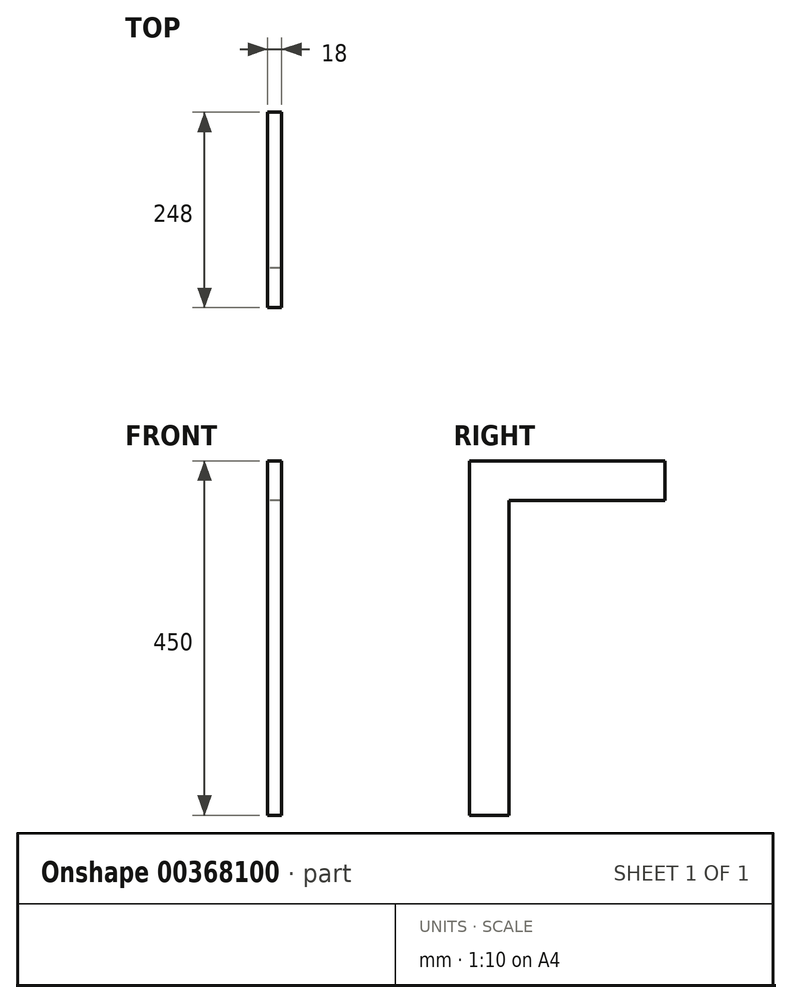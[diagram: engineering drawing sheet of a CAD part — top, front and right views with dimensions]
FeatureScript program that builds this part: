
annotation { "Feature Type Name" : "Feature", "Feature Type Description" : "" }
export const myFeature = defineFeature(function(context is Context, id is Id, definition is map)
    precondition{}
    {
        {
            var Q0;
            Q0=qCreatedBy(makeId("Right.planeOp"),FACE);
            var sketch = newSketch(context, id + "F0", { "sketchPlane" : qUnion([Q0])});
            skLineSegment(sketch, "E0", {"start": v(0, 0) * mm, "end": v(0, 450) * mm});
            skLineSegment(sketch, "E1", {"start": v(0, 450) * mm, "end": v(248, 450) * mm});
            skLineSegment(sketch, "E2", {"start": v(248, 450) * mm, "end": v(248, 400) * mm});
            skLineSegment(sketch, "E3", {"start": v(248, 400) * mm, "end": v(50, 400) * mm});
            skLineSegment(sketch, "E4", {"start": v(50, 400) * mm, "end": v(50, 0) * mm});
            skLineSegment(sketch, "E5", {"start": v(50, 0) * mm, "end": v(0, 0) * mm});
            skSolve(sketch);
        }
        {
            var Q0;
            Q0=makeQuery(id+"F0.imprint","IMPRINT",FACE,{"disambiguationData":[TD([[makeQuery(id+"F0.imprint","IMPRINT",EDGE,{"derivedFrom":sQuery(id+"F0.wireOp",EDGE,"E0")}),-1.0]])]});
            extrude(context, id + "F1", {"entities" : qUnion([Q0]), "depth" : 18 * mm});
        }
    });
